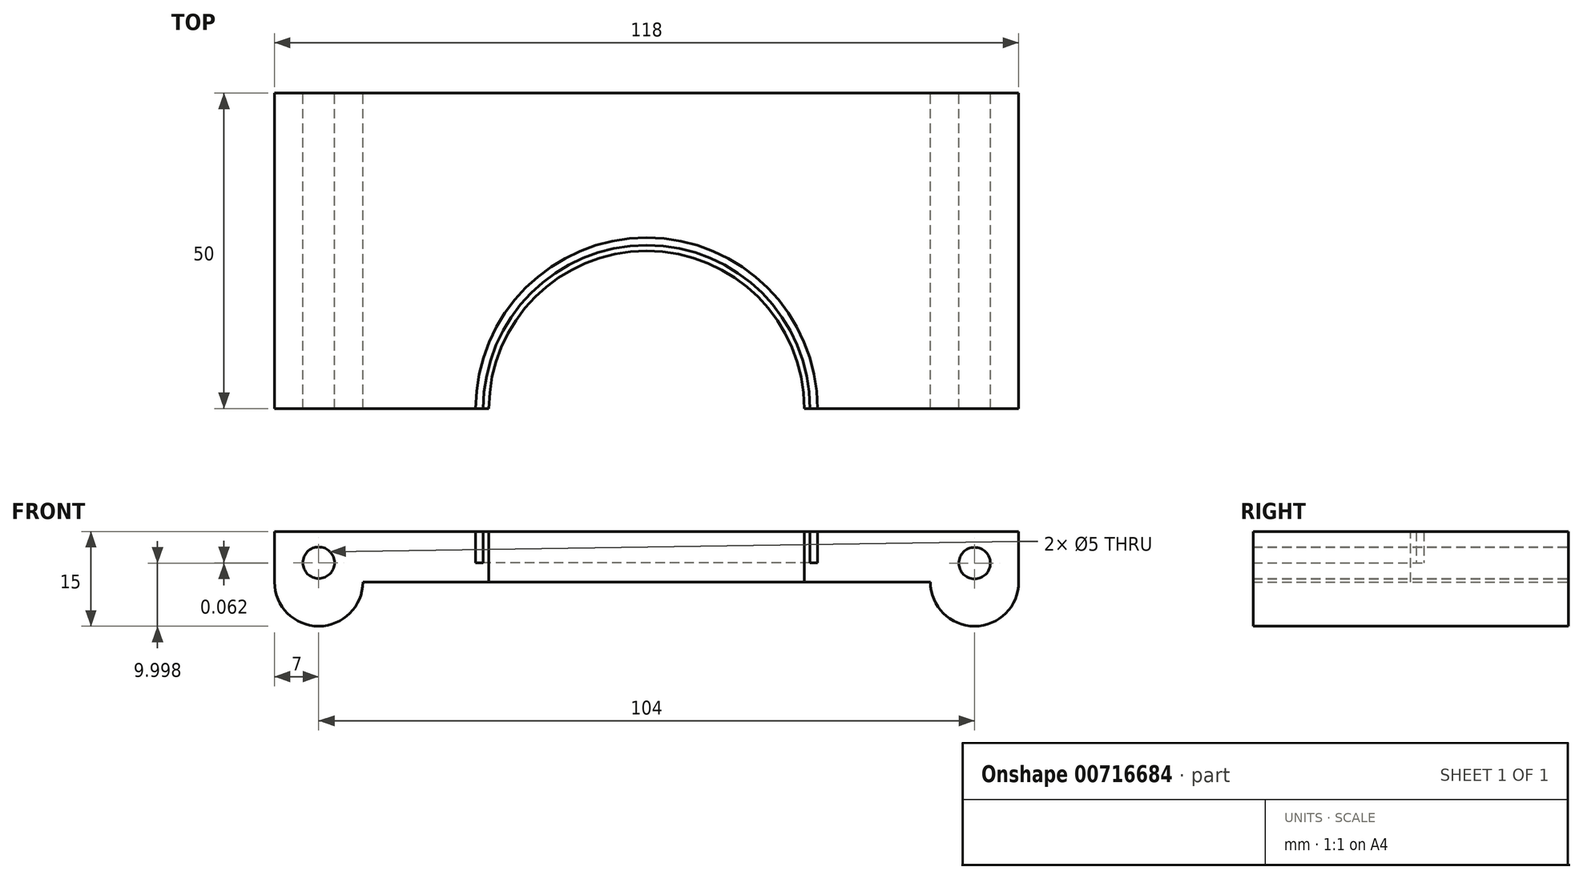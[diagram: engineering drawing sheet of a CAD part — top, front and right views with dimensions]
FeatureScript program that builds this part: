
annotation { "Feature Type Name" : "Feature", "Feature Type Description" : "" }
export const myFeature = defineFeature(function(context is Context, id is Id, definition is map)
    precondition{}
    {
        {
            var Q0;
            Q0=qCreatedBy(makeId("Front.planeOp"),FACE);
            var sketch = newSketch(context, id + "F0", { "sketchPlane" : qUnion([Q0])});
            skLineSegment(sketch, "E0.bottom", {"start": v(0, 4.94) * mm, "end": v(90, 4.94) * mm});
            skLineSegment(sketch, "E0.top", {"start": v(0, -3.06) * mm, "end": v(90, -3.06) * mm});
            skLineSegment(sketch, "E0.left", {"start": v(0, 4.94) * mm, "end": v(0, -3.06) * mm});
            skLineSegment(sketch, "E0.right", {"start": v(90, 4.94) * mm, "end": v(90, -3.06) * mm});
            skLineSegment(sketch, "E1.MirrorCS", {"start": v(90, -0.06) * mm, "end": v(90, -3.06) * mm});
            skLineSegment(sketch, "E2.MirrorCS", {"start": v(104, -0.06) * mm, "end": v(104, -3.06) * mm});
            skArc(sketch, "E3.MirrorCS", {"start": v(104, -3.06) * mm, "mid": v(97, -10.06) * mm, "end": v(90, -3.06) * mm});
            skLineSegment(sketch, "E4.MirrorCS", {"start": v(104, 4.94) * mm, "end": v(104, -3.06) * mm});
            skLineSegment(sketch, "E5.MirrorCS", {"start": v(90, 4.94) * mm, "end": v(104, 4.94) * mm});
            skPoint(sketch, "E6.MirrorCS.start.orphan", {"position": v(90, -0.06) * mm});
            skLineSegment(sketch, "E7.right", {"start": v(-14, 4.94) * mm, "end": v(-14, -3.06) * mm});
            skLineSegment(sketch, "E8.MirrorCS", {"start": v(0, -0.06) * mm, "end": v(0, -3.06) * mm});
            skArc(sketch, "E9.MirrorCS", {"start": v(0, -3.06) * mm, "mid": v(-7, -10.06) * mm, "end": v(-14, -3.06) * mm});
            skLineSegment(sketch, "E10.MirrorCS", {"start": v(-14, 4.94) * mm, "end": v(0, 4.94) * mm});
            skPoint(sketch, "E11.MirrorCS.start.orphan", {"position": v(-14, 4.85) * mm});
            skCircle(sketch, "E12", {"center": v(97, -0.06) * mm, "radius": 2.5 * mm});
            skCircle(sketch, "E13", {"center": v(-7, 0) * mm, "radius": 2.5 * mm});
            skSolve(sketch);
        }
        {
            var Q0;
            Q0=makeQuery(id+"F0.imprint","IMPRINT",FACE,{"disambiguationData":[TD([[makeQuery(id+"F0.imprint","IMPRINT",EDGE,{"derivedFrom":sQuery(id+"F0.wireOp",EDGE,"E0.bottom")}),-1.0]])]});
            var Q1;
            Q1=makeQuery(id+"F0.imprint","IMPRINT",FACE,{"disambiguationData":[TD([[makeQuery(id+"F0.imprint","IMPRINT",EDGE,{"derivedFrom":sQuery(id+"F0.wireOp",EDGE,"E0.left")}),-1.0]])]});
            var Q2;
            Q2 = qSketchRegion(id + "F2", true);
            extrude(context, id + "F1", {"entities" : qUnion([Q0, Q1, Q2]), "depth" : 50 * mm, "offsetDistance" : 25 * mm});
        }
        {
            var Q0;
            Q0=qCreatedBy(makeId("Top.planeOp"),FACE);
            var sketch = newSketch(context, id + "F2", { "sketchPlane" : qUnion([Q0])});
            skCircle(sketch, "E14", {"center": v(45, -50) * mm, "radius": 25 * mm});
            skSolve(sketch);
        }
        {
            var Q0;
            Q0=makeQuery(id+"F2.imprint","IMPRINT",FACE,{"disambiguationData":[TD([[makeQuery(id+"F2.imprint","IMPRINT",EDGE,{"derivedFrom":sQuery(id+"F2.wireOp",EDGE,"E14")}),1.0]])]});
            extrude(context, id + "F3", {"entities" : qUnion([Q0]), "operationType" : NewBodyOperationType.REMOVE, "oppositeDirection" : true, "depth" : 25 * mm, "offsetDistance" : 25 * mm});
        }
        {
            var Q0;
            Q0 = qSketchRegion(id + "F0", true);
            extrude(context, id + "F4", {"entities" : qUnion([Q0]), "operationType" : NewBodyOperationType.ADD, "depth" : 50 * mm, "offsetDistance" : 25 * mm});
        }
        {
            var Q0;
            Q0 = qSketchRegion(id + "F2", true);
            extrude(context, id + "F5", {"entities" : qUnion([Q0]), "operationType" : NewBodyOperationType.REMOVE, "oppositeDirection" : true, "depth" : 25 * mm, "offsetDistance" : 25 * mm});
        }
        {
            var Q0;
            Q0=qCreatedBy(makeId("Top.planeOp"),FACE);
            var sketch = newSketch(context, id + "F6", { "sketchPlane" : qUnion([Q0])});
            skCircle(sketch, "E15", {"center": v(45, -50) * mm, "radius": 25.9 * mm});
            skCircle(sketch, "E16", {"center": v(45, -50) * mm, "radius": 27.1 * mm});
            skSolve(sketch);
        }
        {
            var Q0;
            Q0=makeQuery(id+"F6.imprint","IMPRINT",FACE,{"disambiguationData":[TD([[makeQuery(id+"F6.imprint","IMPRINT",EDGE,{"derivedFrom":sQuery(id+"F6.wireOp",EDGE,"E15")}),-1.0]])]});
            extrude(context, id + "F7", {"entities" : qUnion([Q0]), "operationType" : NewBodyOperationType.REMOVE, "depth" : 5 * mm, "offsetDistance" : 25 * mm});
        }
        {
            var Q0;
            Q0 = qSketchRegion(id + "F2", true);
            extrude(context, id + "F8", {"entities" : qUnion([Q0]), "operationType" : NewBodyOperationType.REMOVE, "depth" : 25 * mm, "offsetDistance" : 25 * mm});
        }
    });
